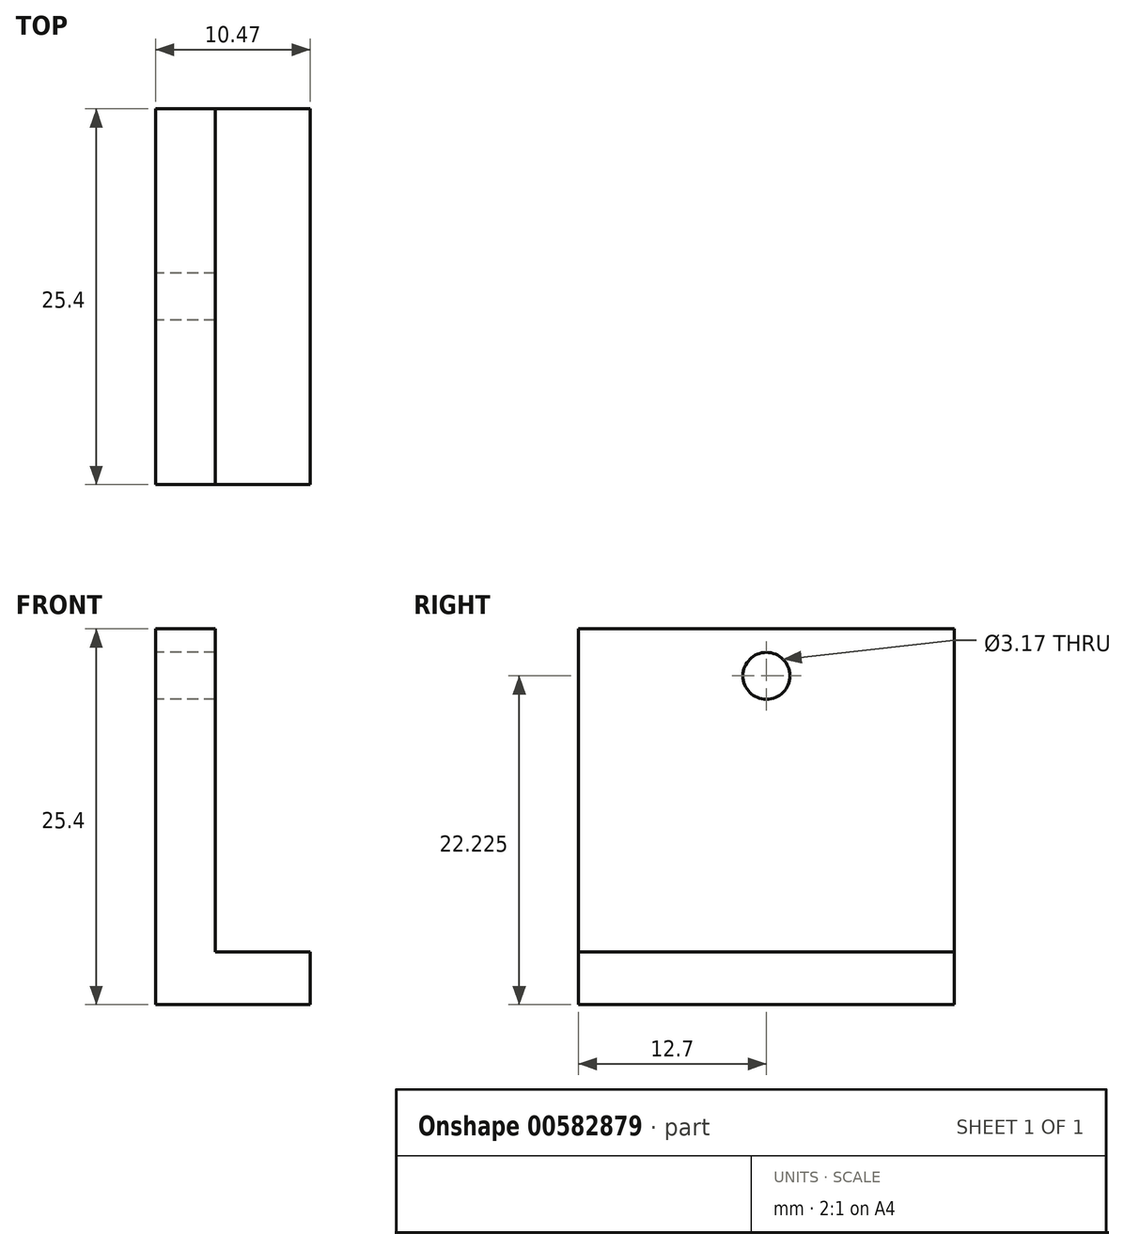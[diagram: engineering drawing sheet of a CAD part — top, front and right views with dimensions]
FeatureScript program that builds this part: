
annotation { "Feature Type Name" : "Feature", "Feature Type Description" : "" }
export const myFeature = defineFeature(function(context is Context, id is Id, definition is map)
    precondition{}
    {
        {
            var Q0;
            Q0=qCreatedBy(makeId("Front.planeOp"),FACE);
            var sketch = newSketch(context, id + "F0", { "sketchPlane" : qUnion([Q0])});
            skLineSegment(sketch, "E0.bottom", {"start": v(0, 0) * mm, "end": v(25.4, 0) * mm});
            skLineSegment(sketch, "E0.top", {"start": v(0, 25.4) * mm, "end": v(25.4, 25.4) * mm});
            skLineSegment(sketch, "E0.left", {"start": v(0, 0) * mm, "end": v(0, 25.4) * mm});
            skLineSegment(sketch, "E0.right", {"start": v(25.4, 0) * mm, "end": v(25.4, 25.4) * mm});
            skSolve(sketch);
        }
        {
            var Q0;
            Q0 = qSketchRegion(id + "F0", true);
            extrude(context, id + "F1", {"entities" : qUnion([Q0]), "depth" : 25.4 * mm, "offsetDistance" : 25.4 * mm});
        }
        {
            var Q0;
            Q0=makeQuery(id+"F1.opExtrude","CAP_FACE",FACE,{"disambiguationData":[OSD([sQuery(id+"F0.wireOp",EDGE,"E0.bottom"),sQuery(id+"F0.wireOp",EDGE,"E0.top"),sQuery(id+"F0.wireOp",EDGE,"E0.left"),sQuery(id+"F0.wireOp",EDGE,"E0.right")])],"isStart":false});
            var sketch = newSketch(context, id + "F2", { "sketchPlane" : qUnion([Q0])});
            skLineSegment(sketch, "E1", {"start": v(7.14, 25.4) * mm, "end": v(7.14, 0) * mm});
            skLineSegment(sketch, "E2", {"start": v(7.14, 0) * mm, "end": v(17.61, 0) * mm});
            skLineSegment(sketch, "E3", {"start": v(17.61, 0) * mm, "end": v(17.61, 3.58) * mm});
            skLineSegment(sketch, "E4", {"start": v(17.61, 3.58) * mm, "end": v(11.19, 3.58) * mm});
            skLineSegment(sketch, "E5", {"start": v(11.19, 3.58) * mm, "end": v(11.19, 25.4) * mm});
            skSolve(sketch);
        }
        {
            var Q0;
            {var subQ0=sQuery(id+"F2.wireOp",EDGE,"E1");Q0=makeQuery(id+"F2.imprint","IMPRINT",FACE,{"disambiguationData":[TD([[makeQuery(id+"F2.imprint","IMPRINT",EDGE,{"derivedFrom":subQ0}),-1.0]])]});}
            var Q1;
            {var subQ2=sQuery(id+"F2.wireOp",EDGE,"E3");Q1=makeQuery(id+"F2.imprint","IMPRINT",FACE,{"disambiguationData":[TD([[makeQuery(id+"F2.imprint","IMPRINT",EDGE,{"derivedFrom":subQ2}),-1.0]])]});}
            extrude(context, id + "F3", {"entities" : qUnion([Q0, Q1]), "operationType" : NewBodyOperationType.REMOVE, "oppositeDirection" : true, "depth" : 25.4 * mm, "offsetDistance" : 25.4 * mm});
        }
        {
            var Q0;
            Q0=makeQuery(id+"F3.boolean.opBoolean","COPY",FACE,{"derivedFrom":makeQuery(id+"F3.opExtrude","SWEPT_FACE",FACE,{"disambiguationData":[OSD([sQuery(id+"F2.wireOp",EDGE,"E1")])]})});
            var sketch = newSketch(context, id + "F4", { "sketchPlane" : qUnion([Q0])});
            skCircle(sketch, "E6", {"center": v(12.7, 22.22) * mm, "radius": 1.59 * mm});
            skSolve(sketch);
        }
        {
            var Q0;
            Q0=makeQuery(id+"F4.imprint","IMPRINT",FACE,{"disambiguationData":[TD([[makeQuery(id+"F4.imprint","IMPRINT",EDGE,{"derivedFrom":sQuery(id+"F4.wireOp",EDGE,"E6")}),1.0]])]});
            extrude(context, id + "F5", {"entities" : qUnion([Q0]), "operationType" : NewBodyOperationType.REMOVE, "oppositeDirection" : true, "depth" : 25.4 * mm, "offsetDistance" : 25.4 * mm});
        }
    });
